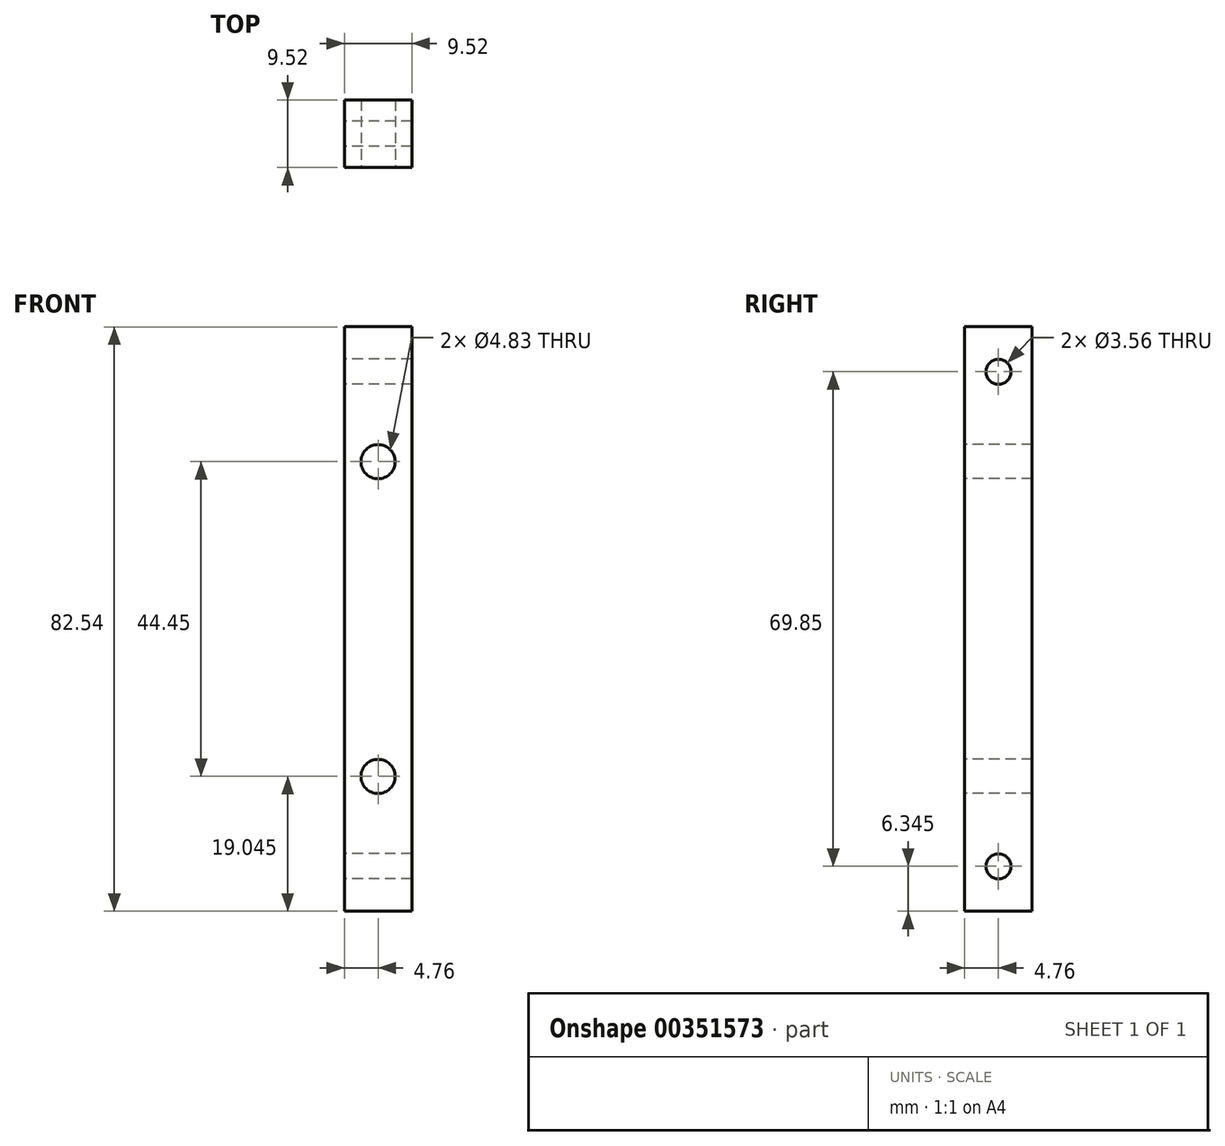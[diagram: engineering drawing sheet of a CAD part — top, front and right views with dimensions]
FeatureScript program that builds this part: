
annotation { "Feature Type Name" : "Feature", "Feature Type Description" : "" }
export const myFeature = defineFeature(function(context is Context, id is Id, definition is map)
    precondition{}
    {
        {
            var Q0;
            Q0=qCreatedBy(makeId("Top.planeOp"),FACE);
            var sketch = newSketch(context, id + "F0", { "sketchPlane" : qUnion([Q0])});
            skLineSegment(sketch, "E0.bottom", {"start": v(4.76, -4.76) * mm, "end": v(-4.76, -4.76) * mm});
            skLineSegment(sketch, "E0.top", {"start": v(4.76, 4.76) * mm, "end": v(-4.76, 4.76) * mm});
            skLineSegment(sketch, "E0.left", {"start": v(4.76, -4.76) * mm, "end": v(4.76, 4.76) * mm});
            skLineSegment(sketch, "E0.right", {"start": v(-4.76, -4.76) * mm, "end": v(-4.76, 4.76) * mm});
            skPoint(sketch, "E0.middle", {"position": v(0, 0) * mm});
            skSolve(sketch);
        }
        {
            var Q0;
            Q0=makeQuery(id+"F0.imprint","IMPRINT",FACE,{"disambiguationData":[TD([[makeQuery(id+"F0.imprint","IMPRINT",EDGE,{"derivedFrom":sQuery(id+"F0.wireOp",EDGE,"E0.bottom")}),-1.0]])]});
            extrude(context, id + "F1", {"entities" : qUnion([Q0]), "depth" : 82.55 * mm, "symmetric" : true});
        }
        {
            var Q0;
            Q0=makeQuery(id+"F1.opExtrude","SWEPT_FACE",FACE,{"disambiguationData":[OSD([sQuery(id+"F0.wireOp",EDGE,"E0.right")])]});
            var sketch = newSketch(context, id + "F2", { "sketchPlane" : qUnion([Q0])});
            skCircle(sketch, "E1", {"center": v(0, -34.93) * mm, "radius": 1.78 * mm});
            skCircle(sketch, "E2.MirrorC", {"center": v(0, 34.93) * mm, "radius": 1.78 * mm});
            skSolve(sketch);
        }
        {
            var Q0;
            Q0 = qSketchRegion(id + "F2", true);
            var Q1;
            Q1=makeQuery(id+"F1.opExtrude","SWEPT_FACE",FACE,{"disambiguationData":[OSD([sQuery(id+"F0.wireOp",EDGE,"E0.left")])]});
            extrude(context, id + "F3", {"entities" : qUnion([Q0]), "operationType" : NewBodyOperationType.REMOVE, "endBound" : BoundingType.UP_TO_SURFACE, "oppositeDirection" : true, "endBoundEntityFace" : qUnion([Q1]), "depth" : 25.4 * mm});
        }
        {
            var Q0;
            Q0=makeQuery(id+"F1.opExtrude","SWEPT_FACE",FACE,{"disambiguationData":[OSD([sQuery(id+"F0.wireOp",EDGE,"E0.bottom")])]});
            var sketch = newSketch(context, id + "F4", { "sketchPlane" : qUnion([Q0])});
            skCircle(sketch, "E3", {"center": v(0, -22.23) * mm, "radius": 2.41 * mm});
            skCircle(sketch, "E4.MirrorC", {"center": v(0, 22.23) * mm, "radius": 2.41 * mm});
            skSolve(sketch);
        }
        {
            var Q0;
            Q0 = qSketchRegion(id + "F4", true);
            var Q1;
            Q1=makeQuery(id+"F1.opExtrude","SWEPT_FACE",FACE,{"disambiguationData":[OSD([sQuery(id+"F0.wireOp",EDGE,"E0.top")])]});
            extrude(context, id + "F5", {"entities" : qUnion([Q0]), "operationType" : NewBodyOperationType.REMOVE, "endBound" : BoundingType.UP_TO_SURFACE, "oppositeDirection" : true, "endBoundEntityFace" : qUnion([Q1]), "depth" : 25.4 * mm});
        }
    });
